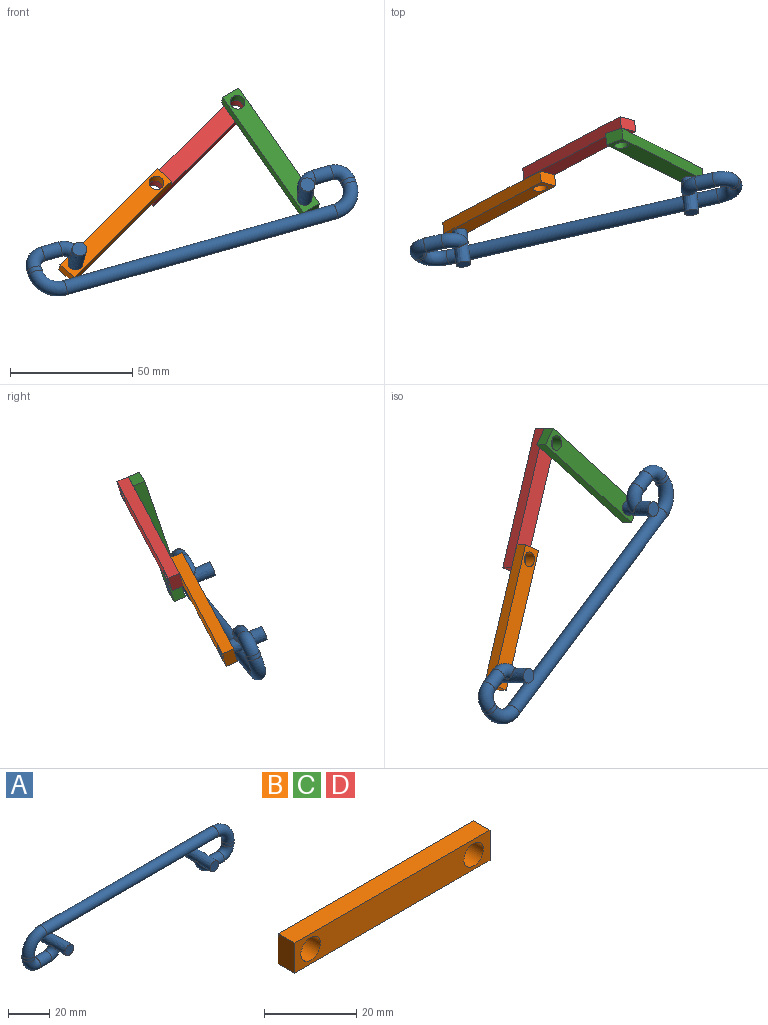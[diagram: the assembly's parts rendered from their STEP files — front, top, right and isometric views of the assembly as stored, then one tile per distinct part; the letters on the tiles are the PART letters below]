
ASSEMBLY  parts=4 mates=4
PART A: 19 faces, bbox 145.7x20.6x25.4 mm
  f0: plane 1.26x0.08mm, normal (0,0,1), area 0.1mm2, adj f1,f7
  f1: torus R=5.48mm, axis (0,1,0), area 133.6mm2, adj f0,f2,f7
  f2: cylinder r=3mm len=7.65mm, axis (-1,0,0), area 144.1mm2, adj f1,f3
  f3: torus R=5.48mm, axis (0,1,0), area 162.3mm2, adj f2,f4
  f4: cylinder r=3mm len=6mm, axis (0,0,1), area 35.6mm2, adj f3,f5
  f5: torus R=9.48mm, axis (0,1,0), area 280.7mm2, adj f4,f6
  f6: cylinder r=3mm len=117.82mm, axis (1,0,0), area 2220.9mm2, adj f5,f15
  f7: bspline ~19.8x6.21mm, area 339.9mm2, adj f0,f1,f8,f9
  f8: plane 6.83x6.83mm, normal (0,1,0), area 28.3mm2, adj f7
  f9: plane 6.83x6.83mm, normal (0,-1,0), area 28.3mm2, adj f7
  f10: plane 1.26x0.08mm, normal (0,0,1), area 0.1mm2, adj f11,f16
  f11: torus R=5.48mm, axis (0,1,0), area 133.6mm2, adj f10,f12,f16
  f12: cylinder r=3mm len=7.65mm, axis (1,0,0), area 144.1mm2, adj f11,f13
  f13: torus R=5.48mm, axis (0,1,0), area 162.3mm2, adj f12,f14
  f14: cylinder r=3mm len=6mm, axis (0,0,1), area 35.6mm2, adj f13,f15
  f15: torus R=9.48mm, axis (0,1,0), area 280.7mm2, adj f6,f14
  f16: bspline ~19.8x6.21mm, area 339.9mm2, adj f10,f11,f17,f18
  f17: plane 6.83x6.83mm, normal (0,1,0), area 28.3mm2, adj f16
  f18: plane 6.83x6.83mm, normal (0,-1,0), area 28.3mm2, adj f16
PART B: 8 faces, bbox 60x5x8 mm
  f0: plane 60x5mm, normal (0,0,1), area 300mm2, adj f1,f5,f6,f7
  f1: plane 8x5mm, normal (-1,0,0), area 40mm2, adj f0,f2,f6,f7
  f2: plane 60x5mm, normal (0,0,-1), area 300mm2, adj f1,f5,f6,f7
  f3: cylinder r=3mm len=6mm, axis (0,1,0), area 94.2mm2, adj f6,f7
  f4: cylinder r=3mm len=6mm, axis (0,1,0), area 94.2mm2, adj f6,f7
  f5: plane 8x5mm, normal (1,0,0), area 40mm2, adj f0,f2,f6,f7
  f6: plane 60x8mm, normal (0,-1,0), area 423.5mm2, adj f0,f1,f2,f3,f4,f5
  f7: plane 60x8mm, normal (0,1,0), area 423.5mm2, adj f0,f1,f2,f3,f4,f5
PART C: same geometry as B
PART D: same geometry as B
PLACE A rot(axis=(-0.08,0.98,-0.19),162.4deg) t=(24.9,146.49,-45.52)mm fixed
PLACE B rot(axis=(-0.14,0.97,-0.18),134.1deg) t=(29.99,115.9,-24.49)mm
PLACE C rot(axis=(-0.06,-0.97,0.22),123.7deg) t=(48.62,93.96,-80.8)mm
PLACE D rot(axis=(-0.14,0.97,-0.18),134.1deg) t=(62.74,138.04,6.53)mm
MATE revolute A.f8 <-> C.f3  axis (-0.1,0.92,-0.39) through (48.14,111.26,-39.98)mm
MATE revolute D.f4 <-> B.f3  axis (0.1,-0.92,0.39) through (-12.59,107.51,-33.53)mm
MATE revolute B.f4 <-> A.f17  axis (-0.1,0.92,-0.39) through (-45.83,89.95,-66.5)mm
MATE revolute C.f4 <-> D.f3  axis (-0.1,0.92,-0.39) through (20.65,125.07,-0.56)mm
